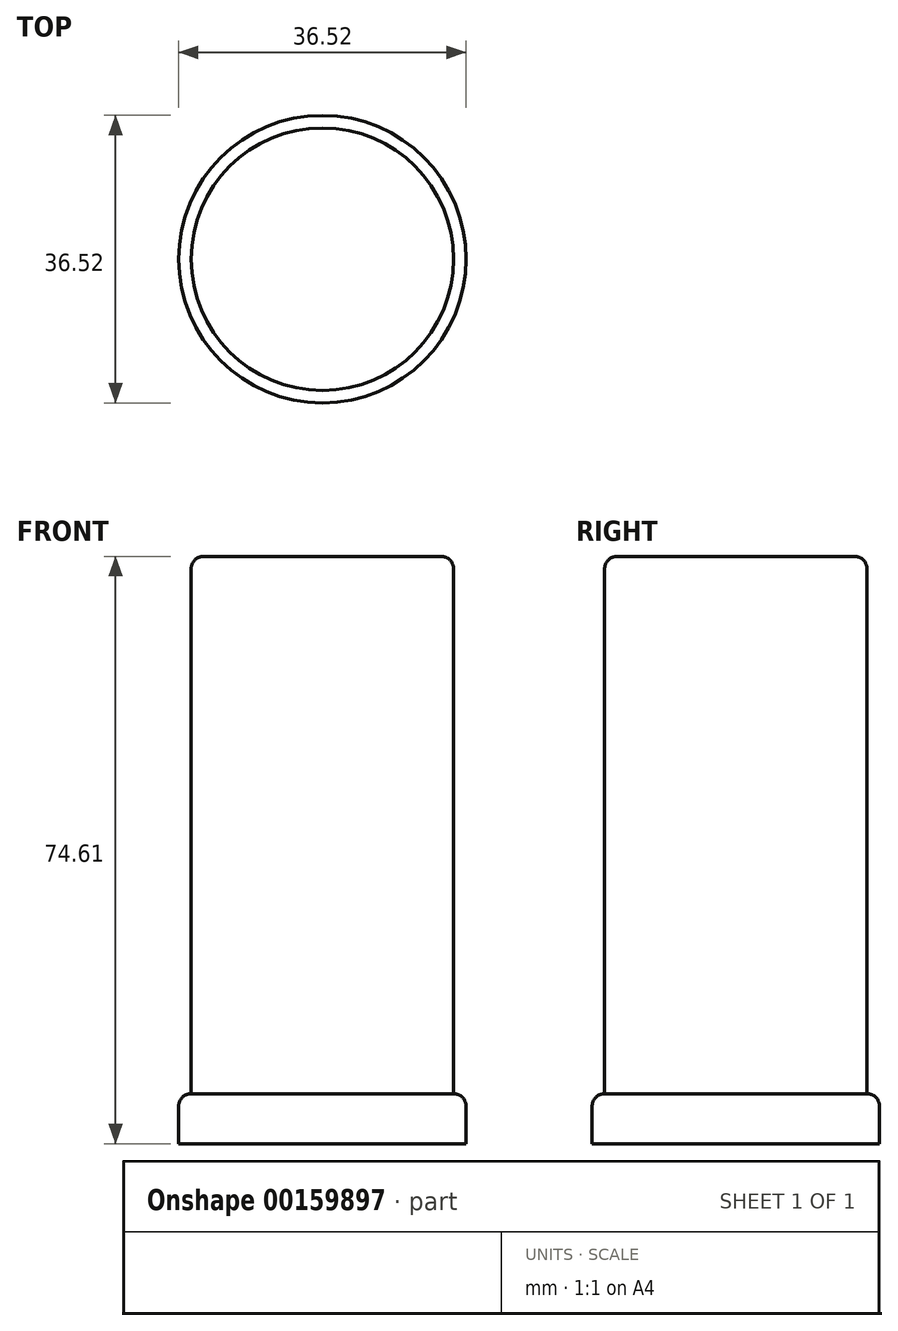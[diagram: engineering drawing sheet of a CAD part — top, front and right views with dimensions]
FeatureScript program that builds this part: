
annotation { "Feature Type Name" : "Feature", "Feature Type Description" : "" }
export const myFeature = defineFeature(function(context is Context, id is Id, definition is map)
    precondition{}
    {
        {
            var Q0;
            Q0=qCreatedBy(makeId("Top.planeOp"),FACE);
            var sketch = newSketch(context, id + "F0", { "sketchPlane" : qUnion([Q0])});
            skCircle(sketch, "E0", {"center": v(0, 0) * mm, "radius": 18.26 * mm});
            skSolve(sketch);
        }
        {
            var Q0;
            Q0=makeQuery(id+"F0.imprint","IMPRINT",FACE,{"disambiguationData":[TD([[makeQuery(id+"F0.imprint","IMPRINT",EDGE,{"derivedFrom":sQuery(id+"F0.wireOp",EDGE,"E0")}),1.0]])]});
            extrude(context, id + "F1", {"entities" : qUnion([Q0]), "depth" : 6.35 * mm});
        }
        {
            var Q0;
            Q0=makeQuery(id+"F1.opExtrude","CAP_FACE",FACE,{"disambiguationData":[OSD([sQuery(id+"F0.wireOp",EDGE,"E0")])],"isStart":false});
            var sketch = newSketch(context, id + "F2", { "sketchPlane" : qUnion([Q0])});
            skCircle(sketch, "E1", {"center": v(0, 0) * mm, "radius": 16.67 * mm});
            skSolve(sketch);
        }
        {
            var Q0;
            Q0=makeQuery(id+"F2.imprint","IMPRINT",FACE,{"disambiguationData":[TD([[makeQuery(id+"F2.imprint","IMPRINT",EDGE,{"derivedFrom":sQuery(id+"F2.wireOp",EDGE,"E1")}),1.0]])]});
            extrude(context, id + "F3", {"entities" : qUnion([Q0]), "operationType" : NewBodyOperationType.ADD, "depth" : 68.26 * mm});
        }
        {
            var Q0;
            Q0=makeQuery(id+"F1.opExtrude","CAP_EDGE",EDGE,{"disambiguationData":[OSD([sQuery(id+"F0.wireOp",EDGE,"E0")])],"isStart":false});
            var Q1;
            Q1=makeQuery(id+"F3.opExtrude","CAP_EDGE",EDGE,{"disambiguationData":[OSD([sQuery(id+"F2.wireOp",EDGE,"E1")])],"isStart":false});
            fillet(context, id + "F4", {"entities" : qUnion([Q0, Q1]), "radius" : 1.59 * mm, "tangentPropagation" : true, "allowEdgeOverflow" : false});
        }
    });
